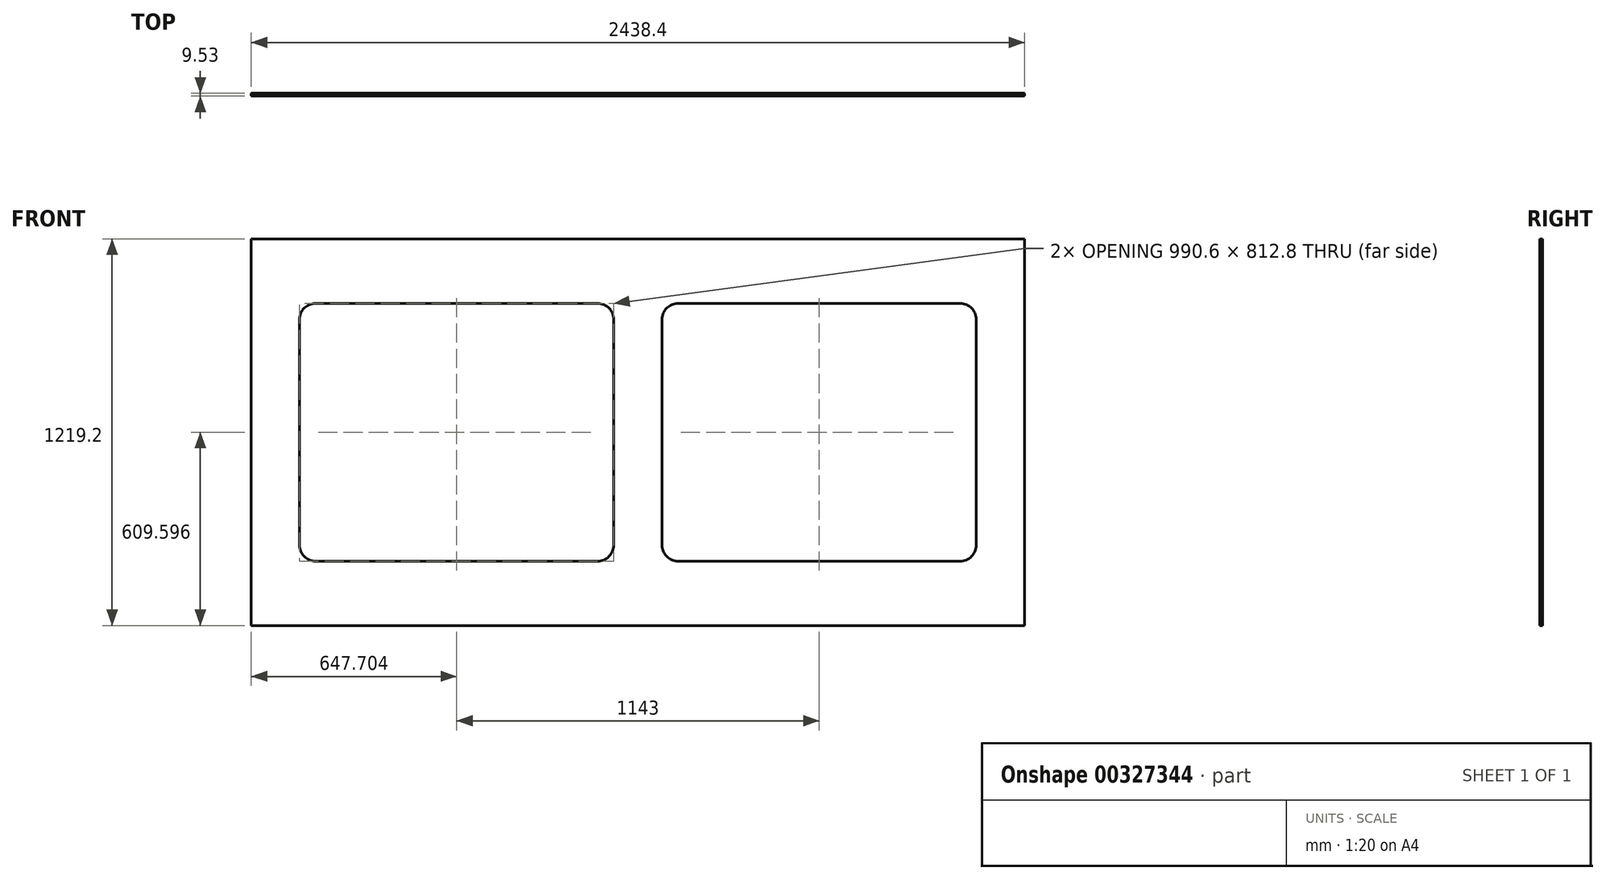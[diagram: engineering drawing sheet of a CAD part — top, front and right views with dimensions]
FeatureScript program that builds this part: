
annotation { "Feature Type Name" : "Feature", "Feature Type Description" : "" }
export const myFeature = defineFeature(function(context is Context, id is Id, definition is map)
    precondition{}
    {
        {
            var Q0;
            Q0=qCreatedBy(makeId("Front.planeOp"),FACE);
            var sketch = newSketch(context, id + "F0", { "sketchPlane" : qUnion([Q0])});
            skLineSegment(sketch, "E0.bottom", {"start": v(-1344.34, 287.15) * mm, "end": v(1094.06, 287.15) * mm});
            skLineSegment(sketch, "E0.top", {"start": v(-1344.34, -932.05) * mm, "end": v(1094.06, -932.05) * mm});
            skLineSegment(sketch, "E0.left", {"start": v(-1344.34, 287.15) * mm, "end": v(-1344.34, -932.05) * mm});
            skLineSegment(sketch, "E0.right", {"start": v(1094.06, 287.15) * mm, "end": v(1094.06, -932.05) * mm});
            skLineSegment(sketch, "E1.bottom", {"start": v(-1141.14, 83.95) * mm, "end": v(-252.14, 83.95) * mm});
            skLineSegment(sketch, "E1.top", {"start": v(-1141.14, -728.85) * mm, "end": v(-252.14, -728.85) * mm});
            skLineSegment(sketch, "E1.left", {"start": v(-1191.94, 33.15) * mm, "end": v(-1191.94, -678.05) * mm});
            skLineSegment(sketch, "E1.right", {"start": v(-201.34, 33.15) * mm, "end": v(-201.34, -678.05) * mm});
            skLineSegment(sketch, "E2.bottom", {"start": v(1.86, 83.95) * mm, "end": v(890.86, 83.95) * mm});
            skLineSegment(sketch, "E2.top", {"start": v(1.86, -728.85) * mm, "end": v(890.86, -728.85) * mm});
            skLineSegment(sketch, "E2.left", {"start": v(-48.94, 33.15) * mm, "end": v(-48.94, -678.05) * mm});
            skLineSegment(sketch, "E2.right", {"start": v(941.66, 33.15) * mm, "end": v(941.66, -678.05) * mm});
            skPoint(sketch, "E3.visualSharp", {"position": v(-1191.94, 83.95) * mm});
            skArc(sketch, "E3.filletArc", {"start": v(-1141.14, 83.95) * mm, "mid": v(-1177.06, 69.07) * mm, "end": v(-1191.94, 33.15) * mm});
            skPoint(sketch, "E4.visualSharp", {"position": v(-201.34, 83.95) * mm});
            skArc(sketch, "E4.filletArc", {"start": v(-201.34, 33.15) * mm, "mid": v(-216.22, 69.07) * mm, "end": v(-252.14, 83.95) * mm});
            skPoint(sketch, "E5.visualSharp", {"position": v(-201.34, -728.85) * mm});
            skArc(sketch, "E5.filletArc", {"start": v(-252.14, -728.85) * mm, "mid": v(-216.22, -713.97) * mm, "end": v(-201.34, -678.05) * mm});
            skPoint(sketch, "E6.visualSharp", {"position": v(-1191.94, -728.85) * mm});
            skArc(sketch, "E6.filletArc", {"start": v(-1191.94, -678.05) * mm, "mid": v(-1177.06, -713.97) * mm, "end": v(-1141.14, -728.85) * mm});
            skPoint(sketch, "E7.visualSharp", {"position": v(-48.94, -728.85) * mm});
            skArc(sketch, "E7.filletArc", {"start": v(-48.94, -678.05) * mm, "mid": v(-34.06, -713.97) * mm, "end": v(1.86, -728.85) * mm});
            skPoint(sketch, "E8.visualSharp", {"position": v(-48.94, 83.95) * mm});
            skArc(sketch, "E8.filletArc", {"start": v(1.86, 83.95) * mm, "mid": v(-34.06, 69.07) * mm, "end": v(-48.94, 33.15) * mm});
            skPoint(sketch, "E9.visualSharp", {"position": v(941.66, 83.95) * mm});
            skArc(sketch, "E9.filletArc", {"start": v(941.66, 33.15) * mm, "mid": v(926.78, 69.07) * mm, "end": v(890.86, 83.95) * mm});
            skPoint(sketch, "E10.visualSharp", {"position": v(941.66, -728.85) * mm});
            skArc(sketch, "E10.filletArc", {"start": v(890.86, -728.85) * mm, "mid": v(926.78, -713.97) * mm, "end": v(941.66, -678.05) * mm});
            skSolve(sketch);
        }
        {
            var Q0;
            Q0 = qSketchRegion(id + "F0", true);
            extrude(context, id + "F1", {"entities" : qUnion([Q0]), "depth" : 9.52 * mm});
        }
    });
